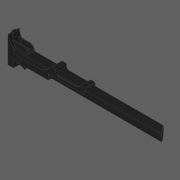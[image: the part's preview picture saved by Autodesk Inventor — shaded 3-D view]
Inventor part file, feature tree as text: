
AUTODESK INVENTOR PART (.ipt)
format: ipt  version: 2020 (Build 240168000, 168)  size: 1,590,784 bytes
history: native  units: in
note: dims shown in document units (in); Inventor stores cm internally (conversion verified against a paired STEP export)
features: other x37, extrude x21, loft x3, pattern_linear x3, fillet x2, sketch x1, projected_geometry x1
ambient origin geometry x8: Origin, YZ Plane, XZ Plane, XY Plane, X Axis, Y Axis, Z Axis, Center Point
bodies: Body1 (feature_tree), Body2 (feature_tree)
feature tree (68):
  other  "CrossSection1"
  other  "CrossSection2"
  other  "CrossSection3"
  other  "Whole"
  other  "Vertical Midplane"
  other  "Horizontal Midplane"
  extrude  "Block"  Depth=0.3937in
  extrude  "Hinge Protrusion"  Depth=0.0197in
  other  "Resonator Profile"
  extrude  "Resonator"  Depth=0.0197in
  extrude  "Resonator Cut"  TaperAngle=0.0deg  [1 undecoded]
  extrude  "Duct Cavity"  Depth=0.4882in
  other  "Duct Cavity Plane"
  loft  "Duct Entrance Loft"
  other  "Whistle Path Midplane"
  other  "Slit Loft To"
  loft  "Slit Loft"
  extrude  "Slit"  TaperAngle=0.0deg  [1 undecoded]
  other  "Fitting"
  extrude  "Edge Cut"  Depth=0.0197in
  other  "Edge Plane"
  other  "Edge Sketch"
  loft  "Edge Loft"
  extrude  "Edge"  TaperAngle=90.0deg  [1 undecoded]
  other  "Edge Cut Plane"
  extrude  "Spring Steel Slot"  Depth=0.0197in
  fillet  "Duct Fillet"  [1 undecoded]
  pattern_linear  "Channel Repetition"  Spacing1=0.2441in  [1 undecoded]
  extrude  "Edge Length Cut"  Depth=0.0197in
  other  "Tube Length Curve"
  extrude  "Long Tubes Length Cut"  Depth=0.0197in
  extrude  "Short Tubes Length Cut"  Depth=0.0197in
  extrude  "Whistle Walls"  Depth=0.0197in
  fillet  "Whistle Wall Fillet"  Radius=0.4921in
  pattern_linear  "Whistle Wall Repetition"  Spacing1=0.0197in  [1 undecoded]
  extrude  "End Caps"  Depth=0.2559in
  extrude  "Extra Block (for short notes)"  Depth=0.0197in
  other  "End Cap Tidying Plane"
  other  "End Cap Tidying Sketch"
  extrude  "End Cap Tidying"  Depth=0.4882in
  extrude  "End Cap Tidying (reverse)"  TaperAngle=0.0deg  [1 undecoded]
  pattern_linear  "End Cap Tidying Repetition"  Spacing1=0.2441in  [1 undecoded]
  extrude  "End Cap Tidying (edges)"  Depth=0.0197in
  extrude  "End Cap Tidying (edges, reverse)"  Depth=0.0197in
  other  "End-of-block Plane"
  extrude  "Manifold Slots"  Depth=0.0197in
  extrude  "Extension for Top C Key"  TaperAngle=0.0deg  [1 undecoded]
  other  "Split Plane"
  other  "Split for Printing"
  other  "Block Profile"
  other  "Fitting Sketch"
  other  "Duct Cavity Profile"
  other  "Duct Entrance Loft From"
  other  "Hinge Protrusion Sketch"
  other  "Edge Cut Sketch"
  other  "Edges3"
  other  "Edge Length Curve"
  other  "Whistle Wall Sketch"
  other  "2D Equation Curve10"
  other  "2D Equation Curve11"
  other  "Duct Entrance Loft To"
  other  "Slit Loft From"
  other  "Manifold Slot Sketch"
  other  "Spring Steel Slot Sketch"
  sketch  "Sketch27"  dims[d6=0.0in d7=0.3937in d9=0.4724in d20=0.3153in d21=0.0in d58=0.4882in d59=0.0in d62=2.3498in d63=0.0in d70=0.1969in d71=0.1292in d80=90.0deg d105=0.2362in d106=0.0in d109=0.2441in d111=0.1528in d112=0.1245in d114=0.1528in d115=0.2441in d118=0.4921in d148=0.0197in d150=0.2559in d151=0.8819in d152=0.4882in d154=0.0in d162=0.2441in d163=0.2362in d165=0.2441in d166=0.2461in d167=0.0in d171=0.2362in d174=0.4882in d175=0.4567in d176=0.0in d177=90.0deg d178=0.0in d179=90.0deg d185=0.3788in d186=0.0in d189=0.1954in d190=28.3465in d191=28.7533in d198=0.0803in d199=0.0in d200=0.0197in d201=0.0787in d202=-0.125in d203=0.7874in d206=0.2559in d209=0.0in d211=0.3937in d213=0.4724in d214=0.2362in d216=0.4567in d217=0.4882in d223=1.5748in d229=0.4882in d230=0.0in d234=0.4724in d235=0.4882in d237=0.2441in d239=1.4483in d240=0.0in d241=0.3937in d243=0.4724in d246=0.0394in d247=0.7043in d248=0.0in d249=0.2441in d250=0.4803in d251=0.0079in d252=28.3465in d253=28.7533in d254=28.3465in d255=28.7533in d256=-0.1575in d257=0.2362in d258=0.2151in d259=0.2441in d261=0.0in d262=90.0deg d263=0.0in d264=90.0deg d265=0.4882in d266=6.7754in d269=0.9992in d270=0.0in d271=0.9992in d272=0.0in d276=0.4882in d277=0.4567in d278=0.4882in d279=0.1954in d280=3.2088in d283=0.2362in d284=0.2441in d285=0.4486in d286=0.5118in d287=0.0in d288=90.0deg d289=0.0in d290=90.0deg d292=0.4882in d293=0.0in d294=1.5748in d295=0.4803in d299=0.5906in d300=0.0in d319=0.1299in d320=0.0787in d321=0.0669in d325=0.1299in d326=0.0787in d327=0.0669in d331=0.1299in d332=0.0787in d333=0.0669in d334=0.1299in d335=0.0787in d336=0.0669in d343=1.8898in d344=1.8898in d345=0.9449in d346=1.4173in d347=0.1299in d348=0.0787in d349=0.0669in d350=0.1299in d351=0.0787in d352=0.0669in d359=1.8898in d375=0.9449in d376=0.1299in d377=0.0787in d378=0.0669in d382=1.8898in d388=0.0317in d389=0.2559in d392=0.2072in d393=0.0in d396=0.2899in d397=0.0197in d398=0.0787in d399=0.0in d400=0.7874in d403=0.0618in d405=0.0197in d406=0.0787in d407=0.0in d408=0.7874in d410=0.1102in d411=0.0in d413=0.1969in d416=0.1095in d417=0.1575in d419=0.4882in d432=0.1412in d434=0.1875in d440=0.2441in d441=0.0in d442=1.5748in d443=0.0157in d444=45.0deg d445=0.4882in d448=0.2441in d451=0.1181in d452=0.5906in d453=0.1969in d457=0.122in d461=0.286in d462=0.0in d137=0.0197in d138=0.0344in d139=0.0197in d140=0.0344in d207=0.0344in d208=0.0197in d267=0.0197in d268=0.0344in d281=0.0197in d282=0.0344in d414=0.0344in d415=0.0197in d425=0.0197in d426=0.0344in d427=0.0197in d428=0.0344in]
  projected_geometry  "Projected Loop5"
  other  "Upper"
  other  "Lower"
note: 9 required parameter values undecoded (feature->parameter linkage not recoverable at this tier; creation-order binding heuristic only, values carry confidence <= 0.55)
